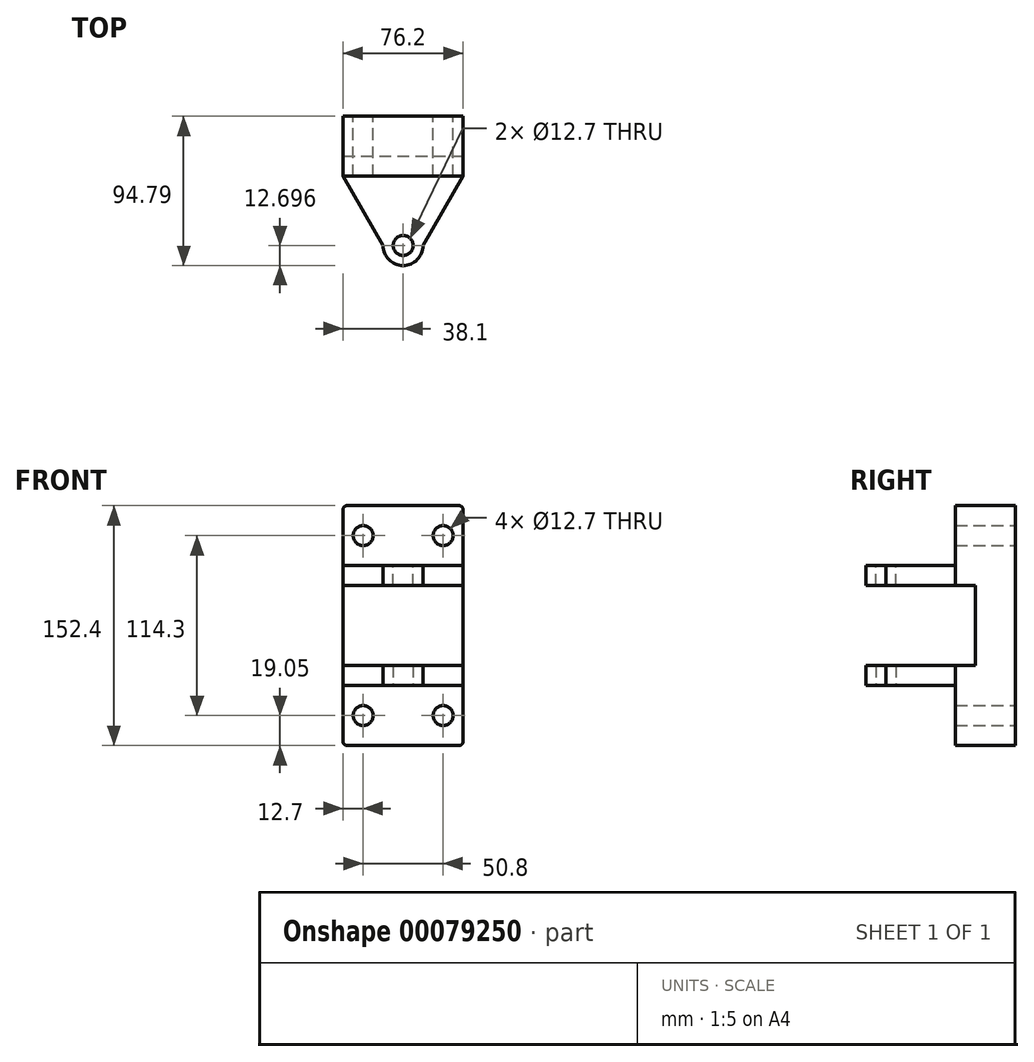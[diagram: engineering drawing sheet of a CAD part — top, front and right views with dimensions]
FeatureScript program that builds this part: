
annotation { "Feature Type Name" : "Feature", "Feature Type Description" : "" }
export const myFeature = defineFeature(function(context is Context, id is Id, definition is map)
    precondition{}
    {
        {
            var Q0;
            Q0=qCreatedBy(makeId("Front.planeOp"),FACE);
            var sketch = newSketch(context, id + "F0", { "sketchPlane" : qUnion([Q0])});
            skLineSegment(sketch, "E0.bottom", {"start": v(-38.1, 76.2) * mm, "end": v(38.1, 76.2) * mm});
            skLineSegment(sketch, "E0.top", {"start": v(-38.1, -76.2) * mm, "end": v(38.1, -76.2) * mm});
            skLineSegment(sketch, "E0.left", {"start": v(-38.1, 76.2) * mm, "end": v(-38.1, -76.2) * mm});
            skLineSegment(sketch, "E0.right", {"start": v(38.1, 76.2) * mm, "end": v(38.1, -76.2) * mm});
            skLineSegment(sketch, "E1.bottom", {"start": v(-38.1, 0) * mm, "end": v(38.1, 0) * mm, "construction": true});
            skLineSegment(sketch, "E1.top", {"start": v(-38.1, 0) * mm, "end": v(38.1, 0) * mm, "construction": true});
            skLineSegment(sketch, "E1.left", {"start": v(-38.1, 0) * mm, "end": v(-38.1, 0) * mm});
            skLineSegment(sketch, "E1.right", {"start": v(38.1, 0) * mm, "end": v(38.1, 0) * mm});
            skLineSegment(sketch, "E2", {"start": v(0, 76.2) * mm, "end": v(0, -76.2) * mm, "construction": true});
            skCircle(sketch, "E3", {"center": v(-25.4, 57.15) * mm, "radius": 6.35 * mm});
            skCircle(sketch, "E4.MirrorC", {"center": v(-25.4, -57.15) * mm, "radius": 6.35 * mm});
            skCircle(sketch, "E5.MirrorC", {"center": v(25.4, 57.15) * mm, "radius": 6.35 * mm});
            skCircle(sketch, "E6.MirrorC", {"center": v(25.4, -57.15) * mm, "radius": 6.35 * mm});
            skSolve(sketch);
        }
        {
            var Q0;
            Q0=makeQuery(id+"F0.imprint","IMPRINT",FACE,{"disambiguationData":[TD([[makeQuery(id+"F0.imprint","IMPRINT",EDGE,{"derivedFrom":sQuery(id+"F0.wireOp",EDGE,"E0.bottom")}),-1.0]])]});
            extrude(context, id + "F1", {"entities" : qUnion([Q0]), "depth" : 25.4 * mm});
        }
        {
            var Q0;
            Q0=makeQuery(id+"F1.opExtrude","SWEPT_EDGE",EDGE,{"disambiguationData":[OSD([sQuery(id+"F0.wireOp",EDGE,"E0.bottom"),sQuery(id+"F0.wireOp",EDGE,"E0.left")])]});
            var Q1;
            Q1=makeQuery(id+"F1.opExtrude","SWEPT_EDGE",EDGE,{"disambiguationData":[OSD([sQuery(id+"F0.wireOp",EDGE,"E0.top"),sQuery(id+"F0.wireOp",EDGE,"E0.left")])]});
            var Q2;
            Q2=makeQuery(id+"F1.opExtrude","SWEPT_EDGE",EDGE,{"disambiguationData":[OSD([sQuery(id+"F0.wireOp",EDGE,"E0.top"),sQuery(id+"F0.wireOp",EDGE,"E0.right")])]});
            var Q3;
            Q3=makeQuery(id+"F1.opExtrude","SWEPT_EDGE",EDGE,{"disambiguationData":[OSD([sQuery(id+"F0.wireOp",EDGE,"E0.bottom"),sQuery(id+"F0.wireOp",EDGE,"E0.right")])]});
            fillet(context, id + "F2", {"entities" : qUnion([Q0, Q1, Q2, Q3]), "radius" : 2.54 * mm, "tangentPropagation" : true, "allowEdgeOverflow" : false});
        }
        {
            var Q0;
            Q0=makeQuery(id+"F1.opExtrude","CAP_FACE",FACE,{"disambiguationData":[OSD([sQuery(id+"F0.wireOp",EDGE,"E0.bottom"),sQuery(id+"F0.wireOp",EDGE,"E0.top"),sQuery(id+"F0.wireOp",EDGE,"E0.left"),sQuery(id+"F0.wireOp",EDGE,"E0.right"),sQuery(id+"F0.wireOp",EDGE,"E3"),sQuery(id+"F0.wireOp",EDGE,"E4.MirrorC"),sQuery(id+"F0.wireOp",EDGE,"E5.MirrorC"),sQuery(id+"F0.wireOp",EDGE,"E6.MirrorC")])],"isStart":false});
            var sketch = newSketch(context, id + "F3", { "sketchPlane" : qUnion([Q0])});
            skLineSegment(sketch, "E7.0.0", {"start": v(35.56, 76.2) * mm, "end": v(-35.56, 76.2) * mm});
            skArc(sketch, "E7.0.1", {"start": v(-35.56, 76.2) * mm, "mid": v(-37.36, 75.46) * mm, "end": v(-38.1, 73.66) * mm});
            skLineSegment(sketch, "E7.0.2", {"start": v(-38.1, 73.66) * mm, "end": v(-38.1, -73.66) * mm});
            skArc(sketch, "E7.0.3", {"start": v(-38.1, -73.66) * mm, "mid": v(-37.36, -75.46) * mm, "end": v(-35.56, -76.2) * mm});
            skLineSegment(sketch, "E7.0.4", {"start": v(-35.56, -76.2) * mm, "end": v(35.56, -76.2) * mm});
            skArc(sketch, "E7.0.5", {"start": v(35.56, -76.2) * mm, "mid": v(37.36, -75.46) * mm, "end": v(38.1, -73.66) * mm});
            skLineSegment(sketch, "E7.0.6", {"start": v(38.1, -73.66) * mm, "end": v(38.1, 73.66) * mm});
            skArc(sketch, "E7.0.7", {"start": v(38.1, 73.66) * mm, "mid": v(37.36, 75.46) * mm, "end": v(35.56, 76.2) * mm});
            skLineSegment(sketch, "E8", {"start": v(-38.1, 38.1) * mm, "end": v(38.1, 38.1) * mm});
            skSolve(sketch);
        }
        {
            var Q0;
            Q0=makeQuery(id+"F3.imprint","IMPRINT",FACE,{"disambiguationData":[TD([[makeQuery(id+"F3.imprint","IMPRINT",EDGE,{"derivedFrom":sQuery(id+"F3.wireOp",EDGE,"E7.0.0")}),-1.0]])]});
            extrude(context, id + "F4", {"entities" : qUnion([Q0]), "depth" : 12.7 * mm});
        }
        {
            var Q0;
            Q0=makeQuery(id+"F4.opExtrude","SWEPT_FACE",FACE,{"disambiguationData":[OSD([sQuery(id+"F3.wireOp",EDGE,"E8")])]});
            var sketch = newSketch(context, id + "F5", { "sketchPlane" : qUnion([Q0])});
            skLineSegment(sketch, "E9", {"start": v(-38.1, 38.1) * mm, "end": v(-12.7, 82.1) * mm});
            skLineSegment(sketch, "E10", {"start": v(-12.7, 82.1) * mm, "end": v(12.7, 82.1) * mm});
            skLineSegment(sketch, "E11", {"start": v(12.7, 82.1) * mm, "end": v(38.1, 38.1) * mm});
            skCircle(sketch, "E12", {"center": v(0, 82.1) * mm, "radius": 12.7 * mm});
            skCircle(sketch, "E13", {"center": v(0, 82.1) * mm, "radius": 6.35 * mm});
            skSolve(sketch);
        }
        {
            var Q0;
            {var subQ0=sQuery(id+"F5.wireOp",EDGE,"E9");Q0=makeQuery(id+"F5.imprint","IMPRINT",FACE,{"disambiguationData":[TD([[makeQuery(id+"F5.imprint","IMPRINT",EDGE,{"derivedFrom":subQ0}),-1.0]])]});}
            var Q1;
            {var subQ1=sQuery(id+"F5.wireOp",EDGE,"E10");var subQ3=sQuery(id+"F5.wireOp",EDGE,"E13");var subQ4=makeQuery(id+"F5.imprint","INTERSECT",VERTEX,{"disambiguationData":[OD(0.0)],"derivedFrom":[subQ1,subQ3]});Q1=makeQuery(id+"F5.imprint","IMPRINT",FACE,{"disambiguationData":[TD([[makeQuery(id+"F5.imprint","IMPRINT",EDGE,{"disambiguationData":[TD([[subQ4,-1.0]])],"derivedFrom":subQ3}),-1.0]])]});}
            var Q2;
            {var subQ1=sQuery(id+"F5.wireOp",EDGE,"E10");var subQ3=sQuery(id+"F5.wireOp",EDGE,"E13");var subQ4=makeQuery(id+"F5.imprint","INTERSECT",VERTEX,{"disambiguationData":[OD(0.0)],"derivedFrom":[subQ1,subQ3]});Q2=makeQuery(id+"F5.imprint","IMPRINT",FACE,{"disambiguationData":[TD([[makeQuery(id+"F5.imprint","IMPRINT",EDGE,{"disambiguationData":[TD([[subQ4,1.0]])],"derivedFrom":subQ3}),-1.0]])]});}
            var Q3;
            {var subQ0=sQuery(id+"F3.wireOp",EDGE,"E8");Q3=makeQuery(id+"F5.imprint","IMPRINT",FACE,{"disambiguationData":[TD([[makeQuery(id+"F5.imprint","IMPRINT",EDGE,{"derivedFrom":makeQuery(id+"F4.opExtrude","CAP_EDGE",EDGE,{"disambiguationData":[OSD([subQ0])],"isStart":true})}),1.0]])]});}
            extrude(context, id + "F6", {"entities" : qUnion([Q0, Q1, Q2, Q3]), "depth" : 12.7 * mm});
        }
        {
            var Q0;
            Q0=makeQuery(id+"F6.opExtrude","SWEPT_BODY",BODY,{"disambiguationData":[OSD([sQuery(id+"F3.wireOp",EDGE,"E7.0.2"),sQuery(id+"F3.wireOp",EDGE,"E7.0.6"),sQuery(id+"F3.wireOp",EDGE,"E8"),sQuery(id+"F5.wireOp",EDGE,"E9"),sQuery(id+"F5.wireOp",EDGE,"E11"),sQuery(id+"F5.wireOp",EDGE,"E12"),sQuery(id+"F5.wireOp",EDGE,"E13")])]});
            var Q1;
            Q1=makeQuery(id+"F4.opExtrude","SWEPT_BODY",BODY,{"disambiguationData":[OSD([sQuery(id+"F0.wireOp",EDGE,"E3"),sQuery(id+"F0.wireOp",EDGE,"E5.MirrorC"),sQuery(id+"F3.wireOp",EDGE,"E7.0.0"),sQuery(id+"F3.wireOp",EDGE,"E7.0.1"),sQuery(id+"F3.wireOp",EDGE,"E7.0.2"),sQuery(id+"F3.wireOp",EDGE,"E7.0.6"),sQuery(id+"F3.wireOp",EDGE,"E7.0.7"),sQuery(id+"F3.wireOp",EDGE,"E8")])]});
            var Q2;
            Q2=qCreatedBy(makeId("Top.planeOp"),FACE);
            mirror(context, id + "F7", {"operationType" : NewBodyOperationType.ADD, "entities" : qUnion([Q0, Q1]), "mirrorPlane" : qUnion([Q2])});
        }
    });
